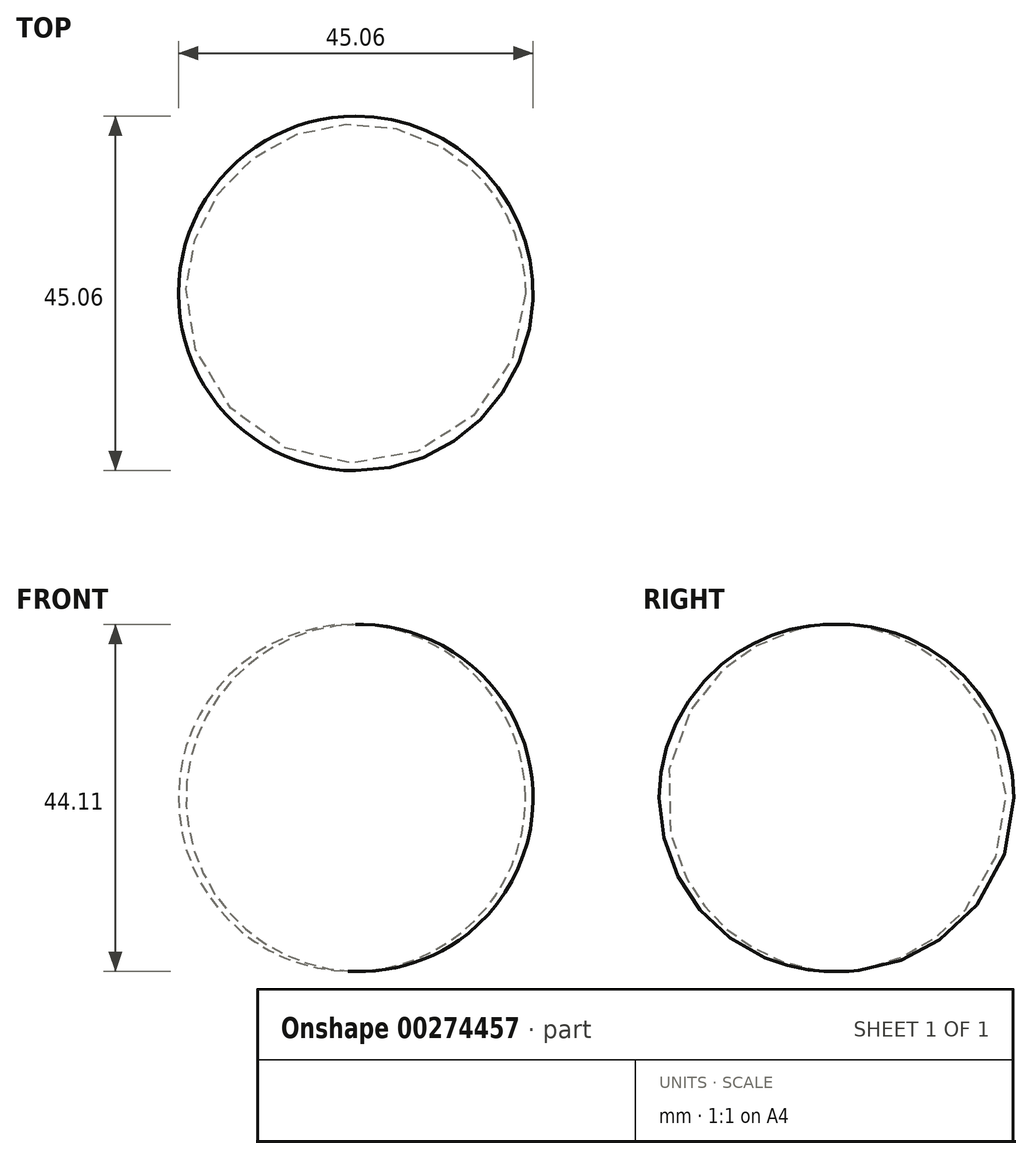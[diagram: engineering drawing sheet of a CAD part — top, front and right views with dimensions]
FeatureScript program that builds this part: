
annotation { "Feature Type Name" : "Feature", "Feature Type Description" : "" }
export const myFeature = defineFeature(function(context is Context, id is Id, definition is map)
    precondition{}
    {
        {
            var Q0;
            Q0=qCreatedBy(makeId("Front.planeOp"),FACE);
            var sketch = newSketch(context, id + "F0", { "sketchPlane" : qUnion([Q0])});
            skArc(sketch, "E0", {"start": v(-45.45, 52.6) * mm, "mid": v(-67.48, 31.04) * mm, "end": v(-46.41, 8.53) * mm});
            skLineSegment(sketch, "E1", {"start": v(-46.41, 8.53) * mm, "end": v(-45.45, 52.6) * mm});
            skSolve(sketch);
        }
        {
            var Q0;
            Q0 = qSketchRegion(id + "F0", true);
            var Q1;
            Q1=sQuery(id+"F0.wireOp",EDGE,"E1");
            revolve(context, id + "F1", {"entities" : qUnion([Q0]), "axis" : qUnion([Q1]), "revolveType" : RevolveType.FULL});
        }
    });
